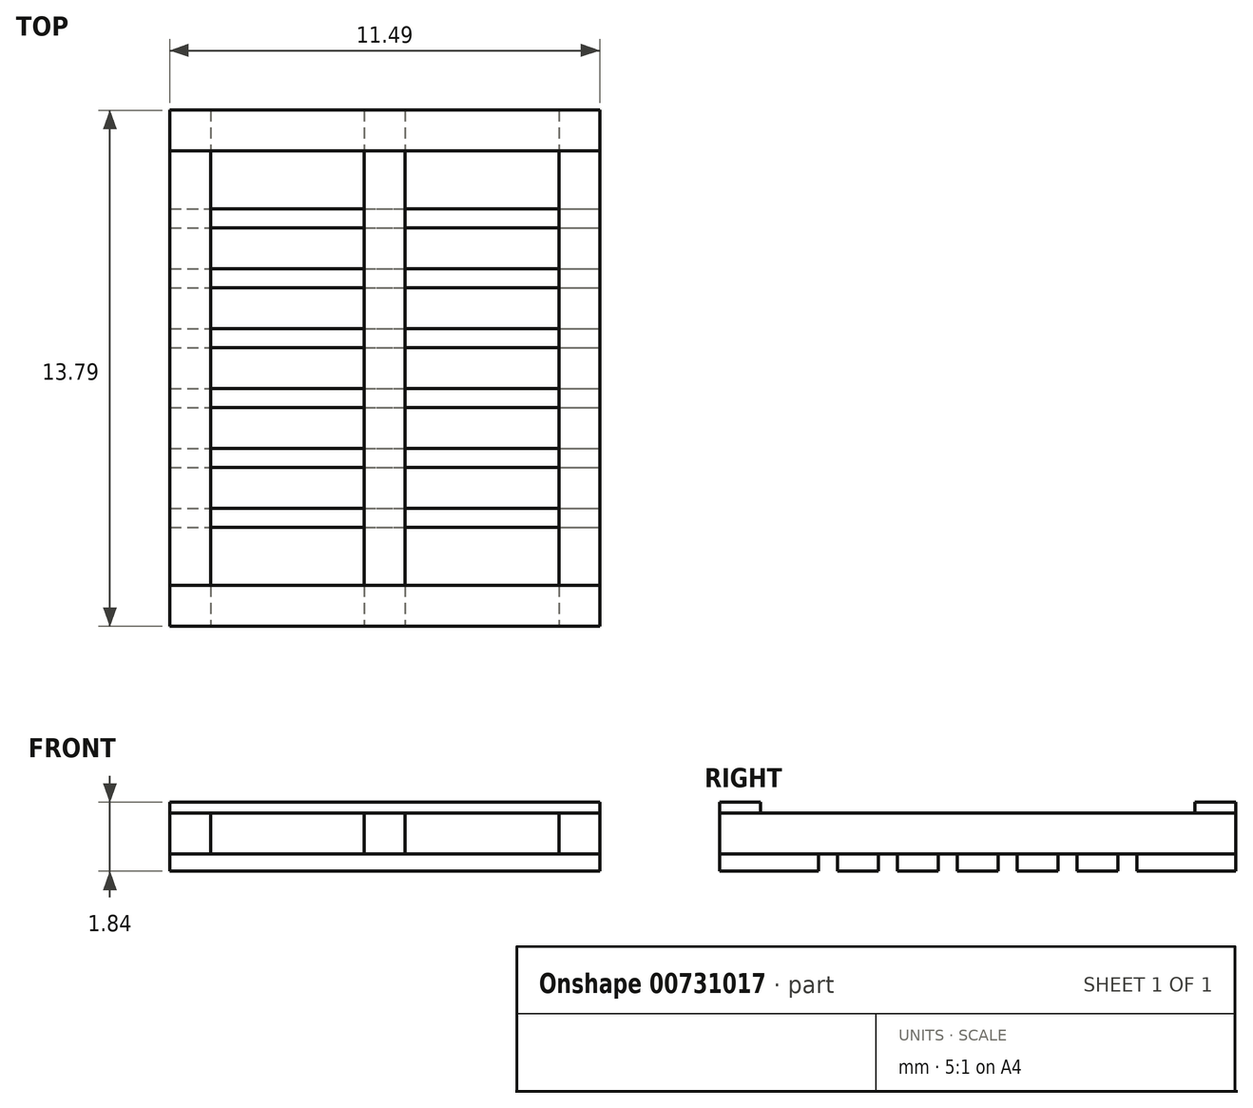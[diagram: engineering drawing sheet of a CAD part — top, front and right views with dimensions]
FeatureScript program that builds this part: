
annotation { "Feature Type Name" : "Feature", "Feature Type Description" : "" }
export const myFeature = defineFeature(function(context is Context, id is Id, definition is map)
    precondition{}
    {
        {
            var Q0;
            Q0=qCreatedBy(makeId("Top.planeOp"),FACE);
            var sketch = newSketch(context, id + "F0", { "sketchPlane" : qUnion([Q0])});
            skLineSegment(sketch, "E0.bottom", {"start": v(0.8, 42.96) * mm, "end": v(12.29, 42.96) * mm});
            skLineSegment(sketch, "E0.top", {"start": v(0.8, 40.32) * mm, "end": v(12.29, 40.32) * mm});
            skLineSegment(sketch, "E0.left", {"start": v(0.8, 42.96) * mm, "end": v(0.8, 40.32) * mm});
            skLineSegment(sketch, "E0.right", {"start": v(12.29, 42.96) * mm, "end": v(12.29, 40.32) * mm});
            skLineSegment(sketch, "E1.bottom", {"start": v(0.8, 39.81) * mm, "end": v(12.3, 39.81) * mm});
            skLineSegment(sketch, "E1.top", {"start": v(0.8, 38.72) * mm, "end": v(12.3, 38.72) * mm});
            skLineSegment(sketch, "E1.left", {"start": v(0.8, 39.81) * mm, "end": v(0.8, 38.72) * mm});
            skLineSegment(sketch, "E1.right", {"start": v(12.3, 39.81) * mm, "end": v(12.3, 38.72) * mm});
            skLineSegment(sketch, "E2.bottom", {"start": v(0.8, 38.21) * mm, "end": v(12.3, 38.21) * mm});
            skLineSegment(sketch, "E2.top", {"start": v(0.8, 37.12) * mm, "end": v(12.3, 37.12) * mm});
            skLineSegment(sketch, "E2.left", {"start": v(0.8, 38.21) * mm, "end": v(0.8, 37.12) * mm});
            skLineSegment(sketch, "E2.right", {"start": v(12.3, 38.21) * mm, "end": v(12.3, 37.12) * mm});
            skLineSegment(sketch, "E3.bottom", {"start": v(0.8, 36.61) * mm, "end": v(12.3, 36.61) * mm});
            skLineSegment(sketch, "E3.top", {"start": v(0.8, 35.52) * mm, "end": v(12.3, 35.52) * mm});
            skLineSegment(sketch, "E3.left", {"start": v(0.8, 36.61) * mm, "end": v(0.8, 35.52) * mm});
            skLineSegment(sketch, "E3.right", {"start": v(12.3, 36.61) * mm, "end": v(12.3, 35.52) * mm});
            skLineSegment(sketch, "E4.bottom", {"start": v(0.8, 35.01) * mm, "end": v(12.3, 35.01) * mm});
            skLineSegment(sketch, "E4.top", {"start": v(0.8, 33.92) * mm, "end": v(12.3, 33.92) * mm});
            skLineSegment(sketch, "E4.left", {"start": v(0.8, 35.01) * mm, "end": v(0.8, 33.92) * mm});
            skLineSegment(sketch, "E4.right", {"start": v(12.3, 35.01) * mm, "end": v(12.3, 33.92) * mm});
            skLineSegment(sketch, "E5.bottom", {"start": v(0.8, 33.41) * mm, "end": v(12.3, 33.41) * mm});
            skLineSegment(sketch, "E5.top", {"start": v(0.8, 32.32) * mm, "end": v(12.3, 32.32) * mm});
            skLineSegment(sketch, "E5.left", {"start": v(0.8, 33.41) * mm, "end": v(0.8, 32.32) * mm});
            skLineSegment(sketch, "E5.right", {"start": v(12.3, 33.41) * mm, "end": v(12.3, 32.32) * mm});
            skLineSegment(sketch, "E6.bottom", {"start": v(0.8, 31.81) * mm, "end": v(12.3, 31.81) * mm});
            skLineSegment(sketch, "E6.top", {"start": v(0.8, 29.17) * mm, "end": v(12.3, 29.17) * mm});
            skLineSegment(sketch, "E6.left", {"start": v(0.8, 31.81) * mm, "end": v(0.8, 29.17) * mm});
            skLineSegment(sketch, "E6.right", {"start": v(12.3, 31.81) * mm, "end": v(12.3, 29.17) * mm});
            skSolve(sketch);
        }
        {
            var Q0;
            Q0=makeQuery(id+"F0.imprint","IMPRINT",FACE,{"disambiguationData":[TD([[makeQuery(id+"F0.imprint","IMPRINT",EDGE,{"derivedFrom":sQuery(id+"F0.wireOp",EDGE,"E6.bottom")}),-1.0]])]});
            var Q1;
            Q1=makeQuery(id+"F0.imprint","IMPRINT",FACE,{"disambiguationData":[TD([[makeQuery(id+"F0.imprint","IMPRINT",EDGE,{"derivedFrom":sQuery(id+"F0.wireOp",EDGE,"E5.bottom")}),-1.0]])]});
            var Q2;
            Q2=makeQuery(id+"F0.imprint","IMPRINT",FACE,{"disambiguationData":[TD([[makeQuery(id+"F0.imprint","IMPRINT",EDGE,{"derivedFrom":sQuery(id+"F0.wireOp",EDGE,"E4.bottom")}),-1.0]])]});
            var Q3;
            Q3=makeQuery(id+"F0.imprint","IMPRINT",FACE,{"disambiguationData":[TD([[makeQuery(id+"F0.imprint","IMPRINT",EDGE,{"derivedFrom":sQuery(id+"F0.wireOp",EDGE,"E3.bottom")}),-1.0]])]});
            var Q4;
            Q4=makeQuery(id+"F0.imprint","IMPRINT",FACE,{"disambiguationData":[TD([[makeQuery(id+"F0.imprint","IMPRINT",EDGE,{"derivedFrom":sQuery(id+"F0.wireOp",EDGE,"E2.bottom")}),-1.0]])]});
            var Q5;
            Q5=makeQuery(id+"F0.imprint","IMPRINT",FACE,{"disambiguationData":[TD([[makeQuery(id+"F0.imprint","IMPRINT",EDGE,{"derivedFrom":sQuery(id+"F0.wireOp",EDGE,"E1.bottom")}),-1.0]])]});
            var Q6;
            Q6=makeQuery(id+"F0.imprint","IMPRINT",FACE,{"disambiguationData":[TD([[makeQuery(id+"F0.imprint","IMPRINT",EDGE,{"derivedFrom":sQuery(id+"F0.wireOp",EDGE,"E0.bottom")}),-1.0]])]});
            extrude(context, id + "F1", {"entities" : qUnion([Q0, Q1, Q2, Q3, Q4, Q5, Q6]), "depth" : 0.46 * mm, "offsetDistance" : 25 * mm});
        }
        {
            var Q0;
            Q0=makeQuery(id+"F1.opExtrude","CAP_FACE",FACE,{"disambiguationData":[OSD([sQuery(id+"F0.wireOp",EDGE,"E0.bottom"),sQuery(id+"F0.wireOp",EDGE,"E0.top"),sQuery(id+"F0.wireOp",EDGE,"E0.left"),sQuery(id+"F0.wireOp",EDGE,"E0.right")])],"isStart":false});
            var sketch = newSketch(context, id + "F2", { "sketchPlane" : qUnion([Q0])});
            skLineSegment(sketch, "E7.bottom", {"start": v(0.8, 42.96) * mm, "end": v(1.89, 42.96) * mm});
            skLineSegment(sketch, "E7.top", {"start": v(0.8, 29.17) * mm, "end": v(1.89, 29.17) * mm});
            skLineSegment(sketch, "E7.left", {"start": v(0.8, 42.96) * mm, "end": v(0.8, 29.17) * mm});
            skLineSegment(sketch, "E7.right", {"start": v(1.89, 42.96) * mm, "end": v(1.89, 29.17) * mm});
            skLineSegment(sketch, "E8.bottom", {"start": v(12.29, 42.96) * mm, "end": v(11.2, 42.96) * mm});
            skLineSegment(sketch, "E8.top", {"start": v(12.29, 29.17) * mm, "end": v(11.2, 29.17) * mm});
            skLineSegment(sketch, "E8.left", {"start": v(12.29, 42.96) * mm, "end": v(12.29, 29.17) * mm});
            skLineSegment(sketch, "E8.right", {"start": v(11.2, 42.96) * mm, "end": v(11.2, 29.17) * mm});
            skLineSegment(sketch, "E9.bottom", {"start": v(6, 42.96) * mm, "end": v(7.09, 42.96) * mm});
            skLineSegment(sketch, "E9.top", {"start": v(6, 29.17) * mm, "end": v(7.09, 29.17) * mm});
            skLineSegment(sketch, "E9.left", {"start": v(6, 42.96) * mm, "end": v(6, 29.17) * mm});
            skLineSegment(sketch, "E9.right", {"start": v(7.09, 42.96) * mm, "end": v(7.09, 29.17) * mm});
            skSolve(sketch);
        }
        {
            var Q0;
            {var subQ0=sQuery(id+"F2.wireOp",EDGE,"E7.top");Q0=makeQuery(id+"F2.imprint","IMPRINT",FACE,{"disambiguationData":[TD([[makeQuery(id+"F2.imprint","IMPRINT",EDGE,{"derivedFrom":subQ0}),1.0]])]});}
            var Q1;
            {var subQ0=sQuery(id+"F2.wireOp",EDGE,"E9.bottom");Q1=makeQuery(id+"F2.imprint","IMPRINT",FACE,{"disambiguationData":[TD([[makeQuery(id+"F2.imprint","IMPRINT",EDGE,{"derivedFrom":subQ0}),-1.0]])]});}
            var Q2;
            {var subQ0=sQuery(id+"F2.wireOp",EDGE,"E9.top");Q2=makeQuery(id+"F2.imprint","IMPRINT",FACE,{"disambiguationData":[TD([[makeQuery(id+"F2.imprint","IMPRINT",EDGE,{"derivedFrom":subQ0}),1.0]])]});}
            var Q3;
            {var subQ0=sQuery(id+"F2.wireOp",EDGE,"E8.bottom");Q3=makeQuery(id+"F2.imprint","IMPRINT",FACE,{"disambiguationData":[TD([[makeQuery(id+"F2.imprint","IMPRINT",EDGE,{"derivedFrom":subQ0}),-1.0]])]});}
            var Q4;
            {var subQ0=sQuery(id+"F2.wireOp",EDGE,"E8.top");Q4=makeQuery(id+"F2.imprint","IMPRINT",FACE,{"disambiguationData":[TD([[makeQuery(id+"F2.imprint","IMPRINT",EDGE,{"derivedFrom":subQ0}),-1.0]])]});}
            var Q5;
            {var subQ0=sQuery(id+"F2.wireOp",EDGE,"E7.bottom");Q5=makeQuery(id+"F2.imprint","IMPRINT",FACE,{"disambiguationData":[TD([[makeQuery(id+"F2.imprint","IMPRINT",EDGE,{"derivedFrom":subQ0}),-1.0]])]});}
            extrude(context, id + "F3", {"entities" : qUnion([Q0, Q1, Q2, Q3, Q4, Q5]), "depth" : 1.09 * mm, "offsetDistance" : 25 * mm});
        }
        {
            var Q0;
            Q0=makeQuery(id+"F3.opExtrude","CAP_FACE",FACE,{"disambiguationData":[OSD([sQuery(id+"F2.wireOp",EDGE,"E7.bottom"),sQuery(id+"F2.wireOp",EDGE,"E7.top"),sQuery(id+"F2.wireOp",EDGE,"E7.left"),sQuery(id+"F2.wireOp",EDGE,"E7.right")])],"isStart":false});
            var sketch = newSketch(context, id + "F4", { "sketchPlane" : qUnion([Q0])});
            skLineSegment(sketch, "E10.bottom", {"start": v(0.8, 42.96) * mm, "end": v(12.29, 42.96) * mm});
            skLineSegment(sketch, "E10.top", {"start": v(0.8, 41.87) * mm, "end": v(12.29, 41.87) * mm});
            skLineSegment(sketch, "E10.left", {"start": v(0.8, 42.96) * mm, "end": v(0.8, 41.87) * mm});
            skLineSegment(sketch, "E10.right", {"start": v(12.29, 42.96) * mm, "end": v(12.29, 41.87) * mm});
            skLineSegment(sketch, "E11.bottom", {"start": v(0.8, 29.17) * mm, "end": v(12.29, 29.17) * mm});
            skLineSegment(sketch, "E11.top", {"start": v(0.8, 30.26) * mm, "end": v(12.29, 30.26) * mm});
            skLineSegment(sketch, "E11.left", {"start": v(0.8, 29.17) * mm, "end": v(0.8, 30.26) * mm});
            skLineSegment(sketch, "E11.right", {"start": v(12.29, 29.17) * mm, "end": v(12.29, 30.26) * mm});
            skLineSegment(sketch, "E12.bottom", {"start": v(0.8, 41.87) * mm, "end": v(1.89, 41.87) * mm});
            skLineSegment(sketch, "E12.top", {"start": v(0.8, 30.26) * mm, "end": v(1.89, 30.26) * mm});
            skLineSegment(sketch, "E12.left", {"start": v(0.8, 41.87) * mm, "end": v(0.8, 30.26) * mm});
            skLineSegment(sketch, "E12.right", {"start": v(1.89, 41.87) * mm, "end": v(1.89, 30.26) * mm});
            skLineSegment(sketch, "E13.bottom", {"start": v(6, 41.87) * mm, "end": v(7.09, 41.87) * mm});
            skLineSegment(sketch, "E13.top", {"start": v(6, 30.26) * mm, "end": v(7.09, 30.26) * mm});
            skLineSegment(sketch, "E13.left", {"start": v(6, 41.87) * mm, "end": v(6, 30.26) * mm});
            skLineSegment(sketch, "E13.right", {"start": v(7.09, 41.87) * mm, "end": v(7.09, 30.26) * mm});
            skLineSegment(sketch, "E14.bottom", {"start": v(12.29, 41.87) * mm, "end": v(11.2, 41.87) * mm});
            skLineSegment(sketch, "E14.top", {"start": v(12.29, 30.26) * mm, "end": v(11.2, 30.26) * mm});
            skLineSegment(sketch, "E14.left", {"start": v(12.29, 41.87) * mm, "end": v(12.29, 30.26) * mm});
            skLineSegment(sketch, "E14.right", {"start": v(11.2, 41.87) * mm, "end": v(11.2, 30.26) * mm});
            skSolve(sketch);
        }
        {
            var Q0;
            Q0=makeQuery(id+"F4.imprint","IMPRINT",FACE,{"disambiguationData":[TD([[makeQuery(id+"F4.imprint","IMPRINT",EDGE,{"derivedFrom":sQuery(id+"F4.wireOp",EDGE,"E12.bottom")}),-1.0]])]});
            var Q1;
            Q1=makeQuery(id+"F4.imprint","IMPRINT",FACE,{"disambiguationData":[TD([[makeQuery(id+"F4.imprint","IMPRINT",EDGE,{"derivedFrom":sQuery(id+"F4.wireOp",EDGE,"E14.bottom")}),1.0]])]});
            var Q2;
            {var subQ0=sQuery(id+"F4.wireOp",EDGE,"E10.left");Q2=makeQuery(id+"F4.imprint","IMPRINT",FACE,{"disambiguationData":[TD([[makeQuery(id+"F4.imprint","IMPRINT",EDGE,{"derivedFrom":subQ0}),1.0]])]});}
            var Q3;
            {var subQ0=sQuery(id+"F4.wireOp",EDGE,"E11.left");Q3=makeQuery(id+"F4.imprint","IMPRINT",FACE,{"disambiguationData":[TD([[makeQuery(id+"F4.imprint","IMPRINT",EDGE,{"derivedFrom":subQ0}),1.0]])]});}
            var Q4;
            {var subQ5=sQuery(id+"F4.wireOp",EDGE,"E11.right");Q4=makeQuery(id+"F4.imprint","IMPRINT",FACE,{"disambiguationData":[TD([[makeQuery(id+"F4.imprint","IMPRINT",EDGE,{"derivedFrom":subQ5}),1.0]])]});}
            var Q5;
            {var subQ0=sQuery(id+"F4.wireOp",EDGE,"E10.right");Q5=makeQuery(id+"F4.imprint","IMPRINT",FACE,{"disambiguationData":[TD([[makeQuery(id+"F4.imprint","IMPRINT",EDGE,{"derivedFrom":subQ0}),-1.0]])]});}
            var Q6;
            Q6=makeQuery(id+"F4.imprint","IMPRINT",FACE,{"disambiguationData":[TD([[makeQuery(id+"F4.imprint","IMPRINT",EDGE,{"derivedFrom":sQuery(id+"F4.wireOp",EDGE,"E13.bottom")}),-1.0]])]});
            extrude(context, id + "F5", {"entities" : qUnion([Q0, Q1, Q2, Q3, Q4, Q5, Q6]), "depth" : 0.29 * mm, "offsetDistance" : 25 * mm});
        }
    });
